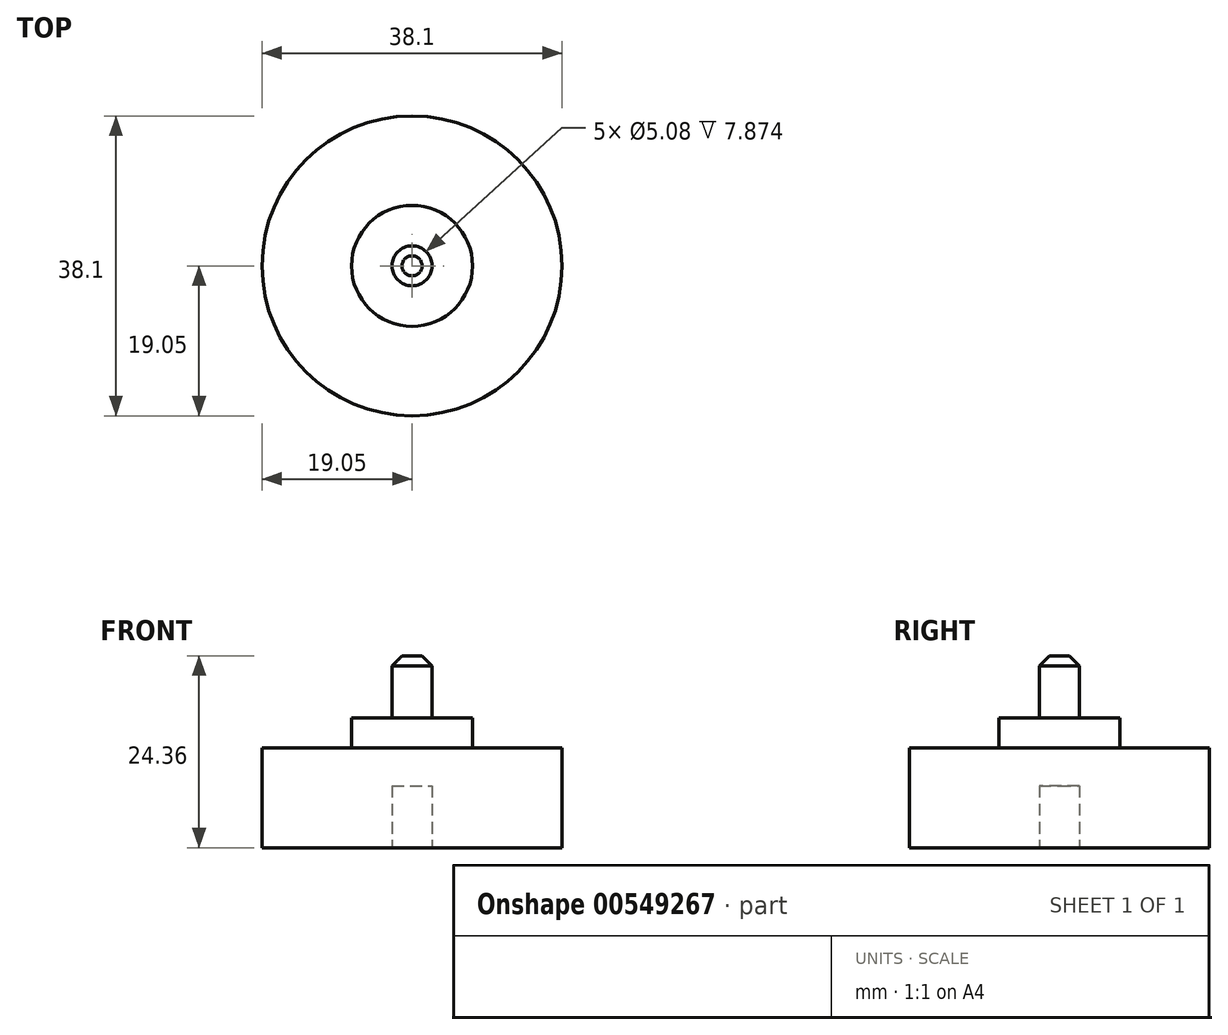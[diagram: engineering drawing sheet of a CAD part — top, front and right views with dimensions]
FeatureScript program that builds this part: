
annotation { "Feature Type Name" : "Feature", "Feature Type Description" : "" }
export const myFeature = defineFeature(function(context is Context, id is Id, definition is map)
    precondition{}
    {
        {
            var Q0;
            Q0=qCreatedBy(makeId("Front.planeOp"),FACE);
            var sketch = newSketch(context, id + "F0", { "sketchPlane" : qUnion([Q0])});
            skLineSegment(sketch, "E0", {"start": v(0, 0) * mm, "end": v(19.05, 0) * mm});
            skLineSegment(sketch, "E1", {"start": v(19.05, 0) * mm, "end": v(19.05, 12.7) * mm});
            skLineSegment(sketch, "E2", {"start": v(19.05, 12.7) * mm, "end": v(7.68, 12.7) * mm});
            skLineSegment(sketch, "E3", {"start": v(2.54, 16.51) * mm, "end": v(7.68, 16.51) * mm});
            skLineSegment(sketch, "E4", {"start": v(7.68, 16.51) * mm, "end": v(7.68, 12.7) * mm});
            skPoint(sketch, "E4.endSnap0", {"position": v(19.05, 6.35) * mm});
            skLineSegment(sketch, "E5", {"start": v(0, 24.36) * mm, "end": v(2.54, 24.36) * mm});
            skLineSegment(sketch, "E6", {"start": v(2.54, 24.36) * mm, "end": v(2.54, 16.51) * mm});
            skPoint(sketch, "E6.endSnap0", {"position": v(3.84, 16.51) * mm});
            skPoint(sketch, "E7.orphan", {"position": v(7.68, 6.35) * mm});
            skPoint(sketch, "E8.start.orphan", {"position": v(0, 12.7) * mm});
            skPoint(sketch, "E9.start.orphan", {"position": v(0, 16.51) * mm});
            skLineSegment(sketch, "E10", {"start": v(0, 0) * mm, "end": v(2.54, 0) * mm});
            skLineSegment(sketch, "E11", {"start": v(2.54, 0) * mm, "end": v(2.54, 7.87) * mm});
            skLineSegment(sketch, "E12", {"start": v(2.54, 7.87) * mm, "end": v(0, 7.87) * mm});
            skLineSegment(sketch, "E13", {"start": v(0, 7.87) * mm, "end": v(0, 24.36) * mm});
            skSolve(sketch);
        }
        {
            var Q0;
            Q0 = qSketchRegion(id + "F0", true);
            var Q1;
            Q1=sQuery(id+"F0.wireOp",EDGE,"E13");
            revolve(context, id + "F1", {"entities" : qUnion([Q0]), "axis" : qUnion([Q1]), "revolveType" : RevolveType.FULL});
        }
        {
            var Q0;
            Q0=makeQuery(id+"F1.opRevolve","SWEPT_EDGE",EDGE,{"disambiguationData":[OSD([sQuery(id+"F0.wireOp",EDGE,"E5"),sQuery(id+"F0.wireOp",EDGE,"E6")])]});
            chamfer(context, id + "F2", {"entities" : qUnion([Q0]), "width" : 1.27 * mm, "tangentPropagation" : true});
        }
    });
